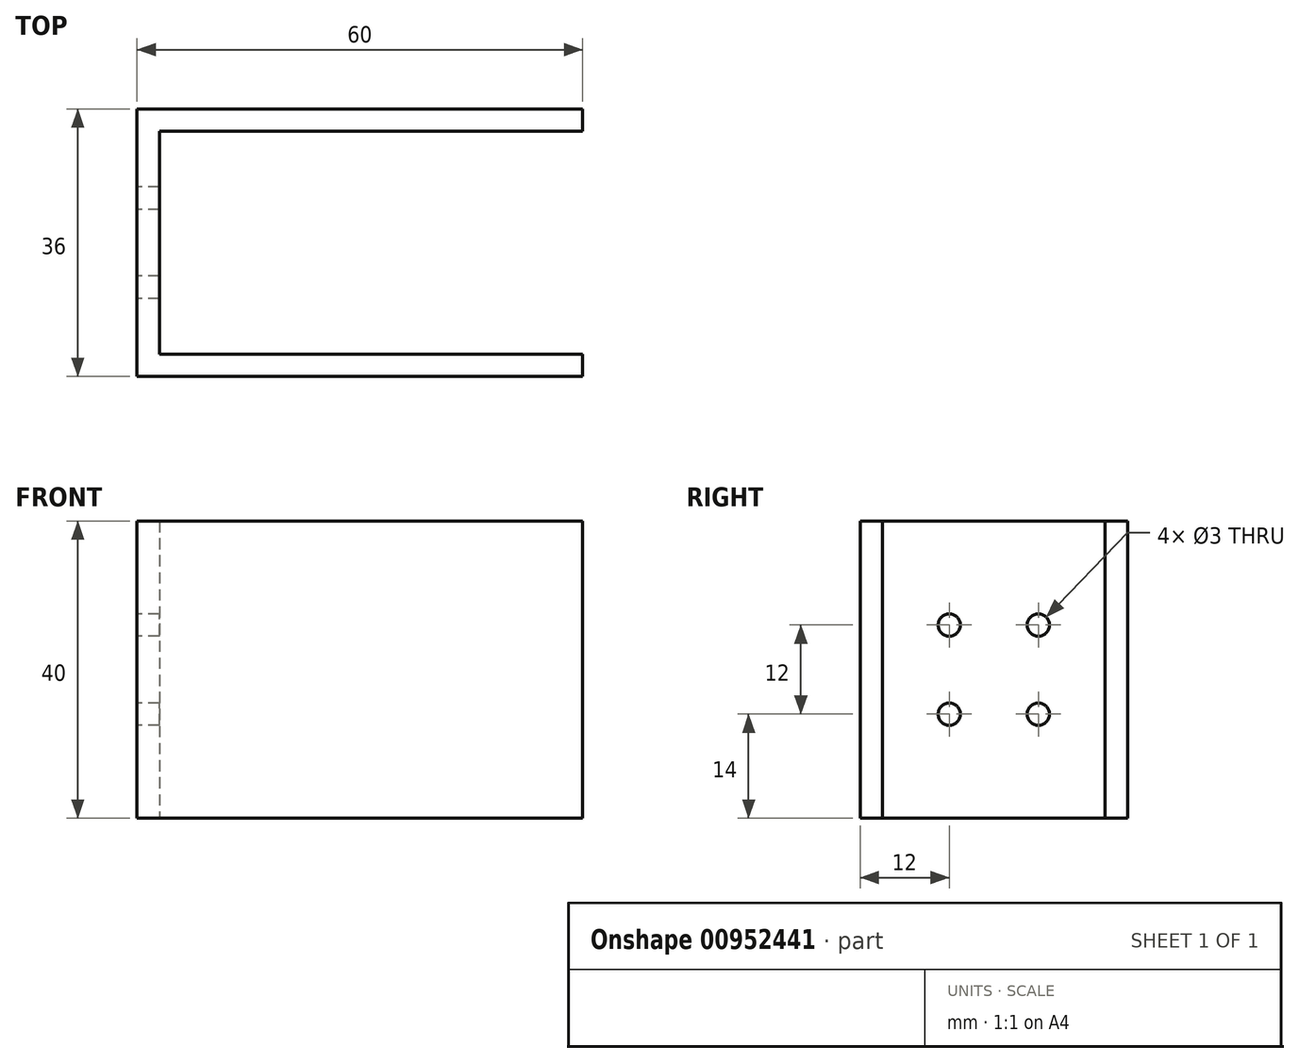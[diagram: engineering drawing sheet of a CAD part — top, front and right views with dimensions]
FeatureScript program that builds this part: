
annotation { "Feature Type Name" : "Feature", "Feature Type Description" : "" }
export const myFeature = defineFeature(function(context is Context, id is Id, definition is map)
    precondition{}
    {
        {
            var Q0;
            Q0=qCreatedBy(makeId("Top.planeOp"),FACE);
            var sketch = newSketch(context, id + "F0", { "sketchPlane" : qUnion([Q0])});
            skLineSegment(sketch, "E0", {"start": v(-39.05, -22.52) * mm, "end": v(-39.05, 13.48) * mm});
            skLineSegment(sketch, "E1", {"start": v(-39.05, 13.48) * mm, "end": v(20.95, 13.48) * mm});
            skLineSegment(sketch, "E2", {"start": v(20.95, 13.48) * mm, "end": v(20.95, 10.48) * mm});
            skLineSegment(sketch, "E3", {"start": v(20.95, 10.48) * mm, "end": v(-36.05, 10.48) * mm});
            skLineSegment(sketch, "E4", {"start": v(-36.05, 10.48) * mm, "end": v(-36.05, -19.52) * mm});
            skLineSegment(sketch, "E5", {"start": v(-36.05, -19.52) * mm, "end": v(20.95, -19.52) * mm});
            skLineSegment(sketch, "E6", {"start": v(20.95, -19.52) * mm, "end": v(20.95, -22.52) * mm});
            skLineSegment(sketch, "E7", {"start": v(20.95, -22.52) * mm, "end": v(-39.05, -22.52) * mm});
            skSolve(sketch);
        }
        {
            var Q0;
            Q0=makeQuery(id+"F0.imprint","IMPRINT",FACE,{"disambiguationData":[TD([[makeQuery(id+"F0.imprint","IMPRINT",EDGE,{"derivedFrom":sQuery(id+"F0.wireOp",EDGE,"E0")}),-1.0]])]});
            extrude(context, id + "F1", {"entities" : qUnion([Q0]), "depth" : 40 * mm, "offsetDistance" : 25 * mm});
        }
        {
            var Q0;
            Q0=makeQuery(id+"F1.opExtrude","SWEPT_FACE",FACE,{"disambiguationData":[OSD([sQuery(id+"F0.wireOp",EDGE,"E0")])]});
            var sketch = newSketch(context, id + "F2", { "sketchPlane" : qUnion([Q0])});
            skCircle(sketch, "E8", {"center": v(-1.48, 26) * mm, "radius": 1.5 * mm});
            skCircle(sketch, "E9", {"center": v(10.52, 26) * mm, "radius": 1.5 * mm});
            skCircle(sketch, "E10", {"center": v(10.52, 14) * mm, "radius": 1.5 * mm});
            skCircle(sketch, "E11", {"center": v(-1.48, 14) * mm, "radius": 1.5 * mm});
            skSolve(sketch);
        }
        {
            var Q0;
            Q0=makeQuery(id+"F2.imprint","IMPRINT",FACE,{"disambiguationData":[TD([[makeQuery(id+"F2.imprint","IMPRINT",EDGE,{"derivedFrom":sQuery(id+"F2.wireOp",EDGE,"E8")}),1.0]])]});
            var Q1;
            Q1=makeQuery(id+"F2.imprint","IMPRINT",FACE,{"disambiguationData":[TD([[makeQuery(id+"F2.imprint","IMPRINT",EDGE,{"derivedFrom":sQuery(id+"F2.wireOp",EDGE,"E9")}),1.0]])]});
            var Q2;
            Q2=makeQuery(id+"F2.imprint","IMPRINT",FACE,{"disambiguationData":[TD([[makeQuery(id+"F2.imprint","IMPRINT",EDGE,{"derivedFrom":sQuery(id+"F2.wireOp",EDGE,"E10")}),1.0]])]});
            var Q3;
            Q3=makeQuery(id+"F2.imprint","IMPRINT",FACE,{"disambiguationData":[TD([[makeQuery(id+"F2.imprint","IMPRINT",EDGE,{"derivedFrom":sQuery(id+"F2.wireOp",EDGE,"E11")}),1.0]])]});
            var Q4;
            Q4=sQuery(id+"F2.wireOp",EDGE,"E8");
            var Q5;
            Q5=sQuery(id+"F2.wireOp",EDGE,"E9");
            var Q6;
            Q6=sQuery(id+"F2.wireOp",EDGE,"E10");
            var Q7;
            Q7=sQuery(id+"F2.wireOp",EDGE,"E11");
            extrude(context, id + "F3", {"entities" : qUnion([Q0, Q1, Q2, Q3]), "operationType" : NewBodyOperationType.REMOVE, "surfaceEntities" : qUnion([Q4, Q5, Q6, Q7]), "oppositeDirection" : true, "depth" : 4 * mm, "offsetDistance" : 25 * mm});
        }
    });
